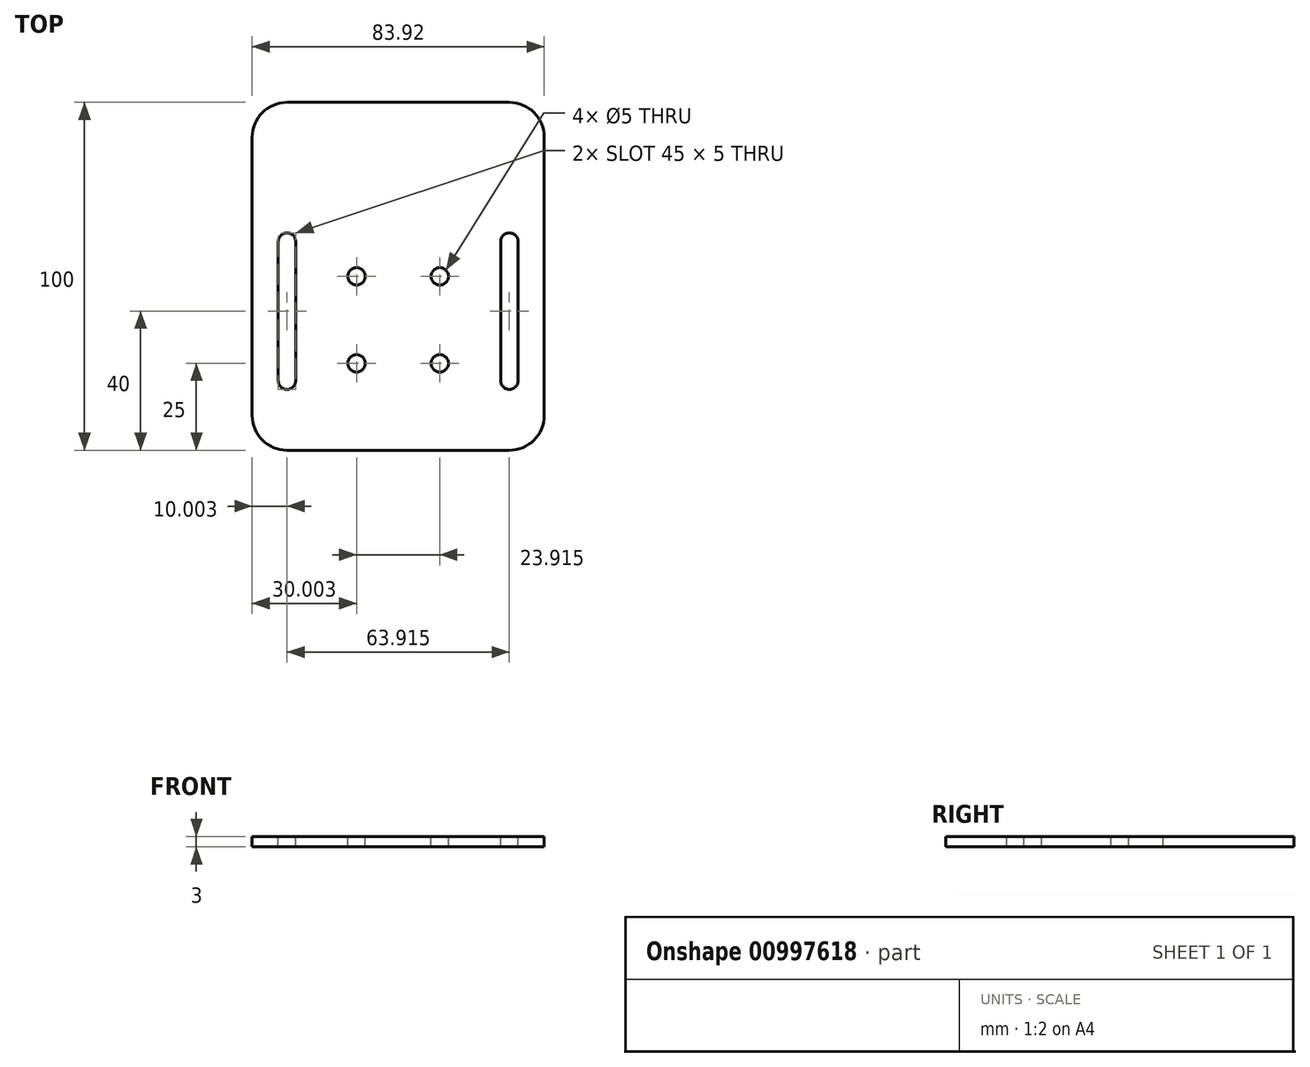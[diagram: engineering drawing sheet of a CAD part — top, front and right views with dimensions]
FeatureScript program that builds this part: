
annotation { "Feature Type Name" : "Feature", "Feature Type Description" : "" }
export const myFeature = defineFeature(function(context is Context, id is Id, definition is map)
    precondition{}
    {
        {
            var Q0;
            Q0=qCreatedBy(makeId("Top.planeOp"),FACE);
            var sketch = newSketch(context, id + "F0", { "sketchPlane" : qUnion([Q0])});
            skLineSegment(sketch, "E0.bottom", {"start": v(0, 0) * mm, "end": v(41.96, 0) * mm});
            skLineSegment(sketch, "E0.top", {"start": v(0, 100) * mm, "end": v(41.96, 100) * mm});
            skLineSegment(sketch, "E0.left", {"start": v(0, 0) * mm, "end": v(0, 100) * mm});
            skLineSegment(sketch, "E0.right", {"start": v(41.96, 0) * mm, "end": v(41.96, 100) * mm});
            skSolve(sketch);
        }
        {
            var Q0;
            Q0 = qSketchRegion(id + "F0", true);
            extrude(context, id + "F1", {"entities" : qUnion([Q0]), "depth" : 3 * mm, "offsetDistance" : 25 * mm});
        }
        {
            var Q0;
            Q0=makeQuery(id+"F1.opExtrude","CAP_FACE",FACE,{"disambiguationData":[OSD([sQuery(id+"F0.wireOp",EDGE,"E0.bottom"),sQuery(id+"F0.wireOp",EDGE,"E0.top"),sQuery(id+"F0.wireOp",EDGE,"E0.left"),sQuery(id+"F0.wireOp",EDGE,"E0.right")])],"isStart":false});
            var sketch = newSketch(context, id + "F2", { "sketchPlane" : qUnion([Q0])});
            skLineSegment(sketch, "E1", {"start": v(11.96, 25) * mm, "end": v(11.96, 50) * mm});
            skPoint(sketch, "E1.endSnap0", {"position": v(0, 50) * mm});
            skSolve(sketch);
        }
        {
            var Q0;
            Q0=sQuery(id+"F2.wireOp",VERTEX,"E1.end");
            var Q1;
            Q1=sQuery(id+"F2.wireOp",VERTEX,"E1.start");
            var Q2;
            Q2=makeQuery(id+"F1.opExtrude","SWEPT_BODY",BODY,{"disambiguationData":[OSD([sQuery(id+"F0.wireOp",EDGE,"E0.bottom"),sQuery(id+"F0.wireOp",EDGE,"E0.top"),sQuery(id+"F0.wireOp",EDGE,"E0.left"),sQuery(id+"F0.wireOp",EDGE,"E0.right")])]});
            hole(context, id + "F3", {"style" : HoleStyle.SIMPLE, "endStyle" : HoleEndStyle.THROUGH, "holeDiameter" : 5 * mm, "majorDiameter" : 5 * mm, "isTappedThrough" : true, "tappedDepth" : 12 * mm, "tapClearance" : 3, "locations" : qUnion([Q0, Q1]), "scope" : qUnion([Q2])});
        }
        {
            var Q0;
            Q0=makeQuery(id+"F1.opExtrude","CAP_FACE",FACE,{"disambiguationData":[OSD([sQuery(id+"F0.wireOp",EDGE,"E0.bottom"),sQuery(id+"F0.wireOp",EDGE,"E0.top"),sQuery(id+"F0.wireOp",EDGE,"E0.left"),sQuery(id+"F0.wireOp",EDGE,"E0.right")])],"isStart":false});
            var sketch = newSketch(context, id + "F4", { "sketchPlane" : qUnion([Q0])});
            skLineSegment(sketch, "E2", {"start": v(31.96, 20) * mm, "end": v(31.96, 60) * mm});
            skSolve(sketch);
        }
        {
            var Q0;
            Q0=makeQuery(id+"F4.imprint","IMPRINT",FACE,{"disambiguationData":[TD([[makeQuery(id+"F4.imprint","IMPRINT",EDGE,{"derivedFrom":makeQuery(id+"F1.opExtrude","CAP_EDGE",EDGE,{"disambiguationData":[OSD([sQuery(id+"F0.wireOp",EDGE,"E0.bottom")])],"isStart":false})}),1.0]])]});
            var sketch = newSketch(context, id + "F5", { "sketchPlane" : qUnion([Q0])});
            skLineSegment(sketch, "E3.JUB.JUB", {"start": v(31.96, 20) * mm, "end": v(31.96, 60) * mm, "construction": true});
            skArc(sketch, "E3.0.startCap", {"start": v(34.46, 20) * mm, "mid": v(31.96, 17.5) * mm, "end": v(29.46, 20) * mm});
            skArc(sketch, "E3.0.endCap", {"start": v(29.46, 60) * mm, "mid": v(31.96, 62.5) * mm, "end": v(34.46, 60) * mm});
            skLineSegment(sketch, "E3.0.left", {"start": v(29.46, 20) * mm, "end": v(29.46, 60) * mm});
            skLineSegment(sketch, "E3.0.right", {"start": v(34.46, 20) * mm, "end": v(34.46, 60) * mm});
            skSolve(sketch);
        }
        {
            var Q0;
            Q0 = qSketchRegion(id + "F5", true);
            extrude(context, id + "F6", {"entities" : qUnion([Q0]), "operationType" : NewBodyOperationType.REMOVE, "oppositeDirection" : true, "depth" : 25 * mm, "offsetDistance" : 25 * mm});
        }
        {
            var Q0;
            Q0=makeQuery(id+"F1.opExtrude","SWEPT_EDGE",EDGE,{"disambiguationData":[OSD([sQuery(id+"F0.wireOp",EDGE,"E0.bottom"),sQuery(id+"F0.wireOp",EDGE,"E0.right")])]});
            var Q1;
            Q1=makeQuery(id+"F1.opExtrude","SWEPT_EDGE",EDGE,{"disambiguationData":[OSD([sQuery(id+"F0.wireOp",EDGE,"E0.top"),sQuery(id+"F0.wireOp",EDGE,"E0.right")])]});
            fillet(context, id + "F7", {"entities" : qUnion([Q0, Q1]), "radius" : 10 * mm, "tangentPropagation" : true, "allowEdgeOverflow" : false});
        }
        {
            var Q0;
            Q0=makeQuery(id+"F1.opExtrude","SWEPT_BODY",BODY,{"disambiguationData":[OSD([sQuery(id+"F0.wireOp",EDGE,"E0.bottom"),sQuery(id+"F0.wireOp",EDGE,"E0.top"),sQuery(id+"F0.wireOp",EDGE,"E0.left"),sQuery(id+"F0.wireOp",EDGE,"E0.right")])]});
            var Q1;
            Q1=qCreatedBy(makeId("Right.planeOp"),FACE);
            mirror(context, id + "F8", {"operationType" : NewBodyOperationType.ADD, "entities" : qUnion([Q0]), "mirrorPlane" : qUnion([Q1])});
        }
    });
